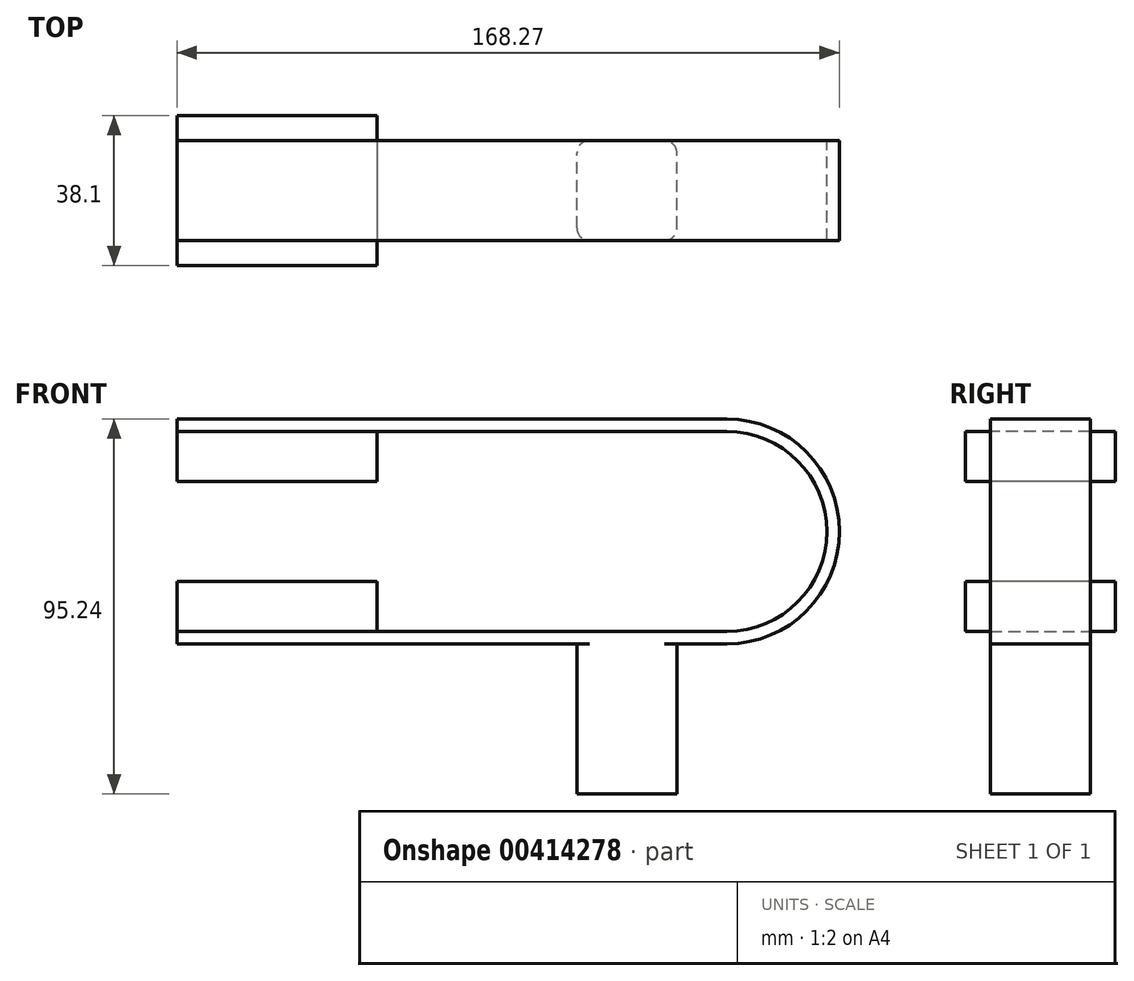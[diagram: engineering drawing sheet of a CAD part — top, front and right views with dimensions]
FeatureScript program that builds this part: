
annotation { "Feature Type Name" : "Feature", "Feature Type Description" : "" }
export const myFeature = defineFeature(function(context is Context, id is Id, definition is map)
    precondition{}
    {
        {
            var Q0;
            Q0=qCreatedBy(makeId("Front.planeOp"),FACE);
            var sketch = newSketch(context, id + "F0", { "sketchPlane" : qUnion([Q0])});
            skArc(sketch, "E0", {"start": v(0, -25.4) * mm, "mid": v(25.4, 0) * mm, "end": v(0, 25.4) * mm});
            skLineSegment(sketch, "E1.bottom", {"start": v(0, 25.4) * mm, "end": v(-139.7, 25.4) * mm});
            skLineSegment(sketch, "E1.top", {"start": v(0, -25.4) * mm, "end": v(-139.7, -25.4) * mm});
            skLineSegment(sketch, "E2.0", {"start": v(0, 28.58) * mm, "end": v(-139.7, 28.57) * mm});
            skArc(sketch, "E2.1", {"start": v(0, -28.58) * mm, "mid": v(28.58, 0) * mm, "end": v(0, 28.58) * mm});
            skLineSegment(sketch, "E2.2", {"start": v(0, -28.57) * mm, "end": v(-139.7, -28.58) * mm});
            skLineSegment(sketch, "E3", {"start": v(-139.7, 25.4) * mm, "end": v(-139.7, 28.57) * mm});
            skLineSegment(sketch, "E4", {"start": v(-139.7, -25.4) * mm, "end": v(-139.7, -28.58) * mm});
            skSolve(sketch);
        }
        {
            var Q0;
            Q0 = qSketchRegion(id + "F0", true);
            extrude(context, id + "F1", {"entities" : qUnion([Q0]), "depth" : 25.4 * mm});
        }
        {
            var Q0;
            Q0=makeQuery(id+"F1.opExtrude","SWEPT_FACE",FACE,{"disambiguationData":[OSD([sQuery(id+"F0.wireOp",EDGE,"E3")])]});
            var sketch = newSketch(context, id + "F2", { "sketchPlane" : qUnion([Q0])});
            skLineSegment(sketch, "E5.bottom", {"start": v(-6.35, 25.4) * mm, "end": v(31.75, 25.4) * mm});
            skLineSegment(sketch, "E5.top", {"start": v(-6.35, 12.7) * mm, "end": v(31.75, 12.7) * mm});
            skLineSegment(sketch, "E5.left", {"start": v(-6.35, 25.4) * mm, "end": v(-6.35, 12.7) * mm});
            skLineSegment(sketch, "E5.right", {"start": v(31.75, 25.4) * mm, "end": v(31.75, 12.7) * mm});
            skLineSegment(sketch, "E6.bottom", {"start": v(-6.35, -12.7) * mm, "end": v(31.75, -12.7) * mm});
            skLineSegment(sketch, "E6.top", {"start": v(-6.35, -25.4) * mm, "end": v(31.75, -25.4) * mm});
            skLineSegment(sketch, "E6.left", {"start": v(-6.35, -12.7) * mm, "end": v(-6.35, -25.4) * mm});
            skLineSegment(sketch, "E6.right", {"start": v(31.75, -12.7) * mm, "end": v(31.75, -25.4) * mm});
            skSolve(sketch);
        }
        {
            var Q0;
            Q0 = qSketchRegion(id + "F2", true);
            extrude(context, id + "F3", {"entities" : qUnion([Q0]), "operationType" : NewBodyOperationType.ADD, "oppositeDirection" : true, "depth" : 50.8 * mm});
        }
        {
            var Q0;
            Q0=makeQuery(id+"F1.opExtrude","SWEPT_FACE",FACE,{"disambiguationData":[OSD([sQuery(id+"F0.wireOp",EDGE,"E2.2")])]});
            var sketch = newSketch(context, id + "F4", { "sketchPlane" : qUnion([Q0])});
            skLineSegment(sketch, "E7.bottom", {"start": v(-38.1, 25.4) * mm, "end": v(-12.7, 25.4) * mm});
            skLineSegment(sketch, "E7.top", {"start": v(-38.1, 0) * mm, "end": v(-12.7, 0) * mm});
            skLineSegment(sketch, "E7.left", {"start": v(-38.1, 25.4) * mm, "end": v(-38.1, 0) * mm});
            skLineSegment(sketch, "E7.right", {"start": v(-12.7, 25.4) * mm, "end": v(-12.7, 0) * mm});
            skSolve(sketch);
        }
        {
            var Q0;
            Q0 = qSketchRegion(id + "F4", true);
            extrude(context, id + "F5", {"entities" : qUnion([Q0]), "operationType" : NewBodyOperationType.ADD, "depth" : 38.1 * mm});
        }
        {
            var Q0;
            Q0=makeQuery(id+"F5.opExtrude","SWEPT_EDGE",EDGE,{"disambiguationData":[OSD([sQuery(id+"F0.wireOp",EDGE,"E2.2"),sQuery(id+"F4.wireOp",EDGE,"E7.bottom"),sQuery(id+"F4.wireOp",EDGE,"E7.left")])]});
            var Q1;
            Q1=makeQuery(id+"F5.opExtrude","SWEPT_EDGE",EDGE,{"disambiguationData":[OSD([sQuery(id+"F0.wireOp",EDGE,"E2.2"),sQuery(id+"F4.wireOp",EDGE,"E7.top"),sQuery(id+"F4.wireOp",EDGE,"E7.left")])]});
            var Q2;
            Q2=makeQuery(id+"F5.opExtrude","SWEPT_EDGE",EDGE,{"disambiguationData":[OSD([sQuery(id+"F0.wireOp",EDGE,"E2.2"),sQuery(id+"F4.wireOp",EDGE,"E7.bottom"),sQuery(id+"F4.wireOp",EDGE,"E7.right")])]});
            var Q3;
            Q3=makeQuery(id+"F5.opExtrude","SWEPT_EDGE",EDGE,{"disambiguationData":[OSD([sQuery(id+"F0.wireOp",EDGE,"E2.2"),sQuery(id+"F4.wireOp",EDGE,"E7.top"),sQuery(id+"F4.wireOp",EDGE,"E7.right")])]});
            fillet(context, id + "F6", {"entities" : qUnion([Q0, Q1, Q2, Q3]), "radius" : 3.17 * mm, "tangentPropagation" : true, "allowEdgeOverflow" : false});
        }
    });
